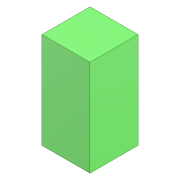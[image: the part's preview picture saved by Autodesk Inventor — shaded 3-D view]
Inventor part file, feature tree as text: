
AUTODESK INVENTOR PART (.ipt)
format: ipt  version: 2022 (Build 260153000, 153)  size: 103,424 bytes
history: native  units: mm
features: extrude x1, shell x1, fillet x1, sketch x1
ambient origin geometry x8: Origin, YZ Plane, XZ Plane, XY Plane, X Axis, Y Axis, Z Axis, Center Point
bodies: Solid1 (feature_tree)
feature tree (4):
  extrude  "Extrusion1"  Depth=50.0mm
  shell  "Shell1"  Thickness=100.0mm
  fillet  "Fillet1"  Radius=5.0mm
  sketch  "Sketch1"  dims[d0=50.0mm d1=50.0mm d2=100.0mm d3=0.0mm d4=5.0mm d5=10.0mm]
